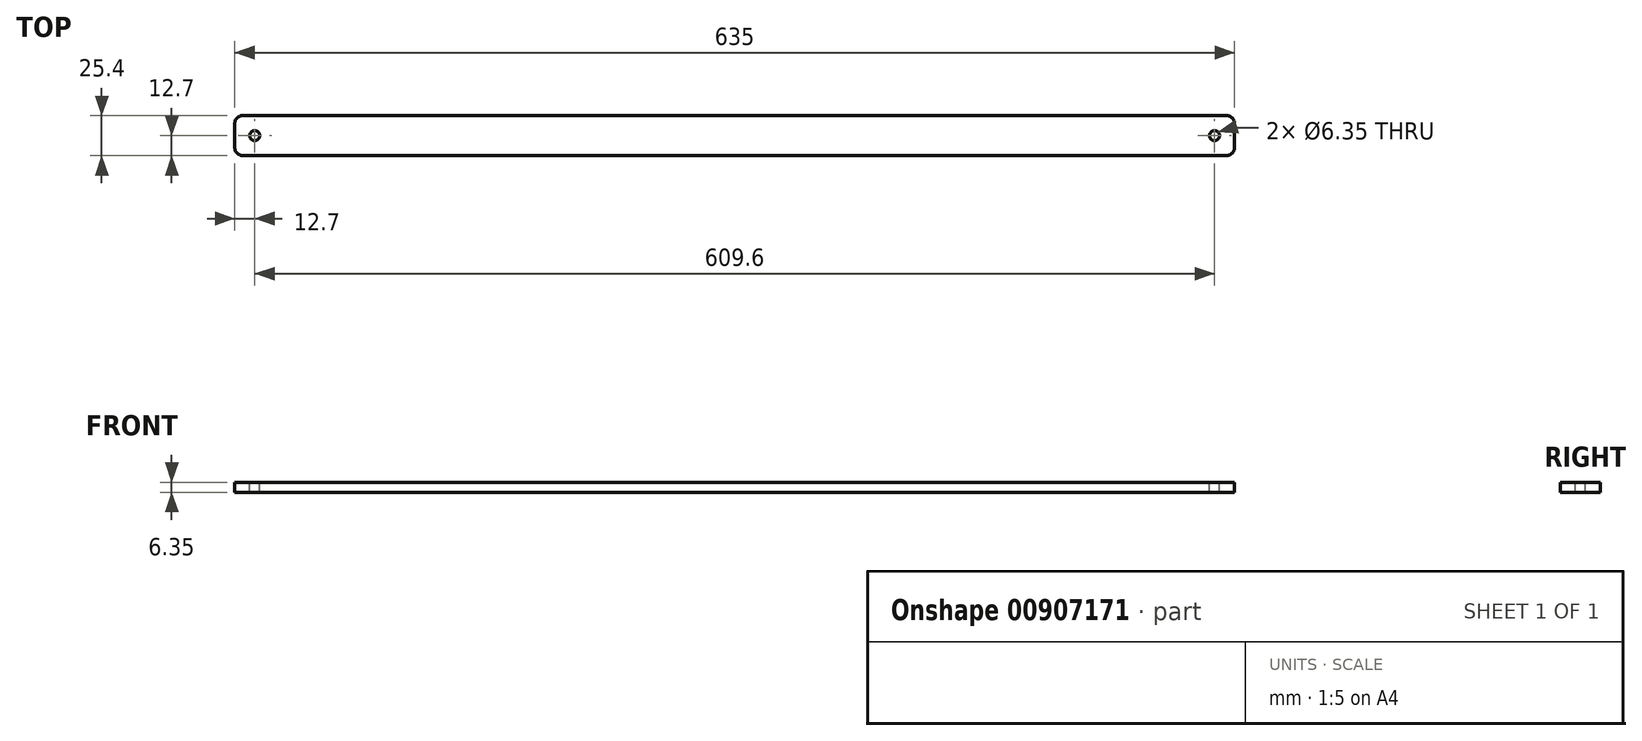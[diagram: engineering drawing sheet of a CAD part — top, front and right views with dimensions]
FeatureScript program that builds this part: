
annotation { "Feature Type Name" : "Feature", "Feature Type Description" : "" }
export const myFeature = defineFeature(function(context is Context, id is Id, definition is map)
    precondition{}
    {
        {
            var Q0;
            Q0=qCreatedBy(makeId("Top.planeOp"),FACE);
            var sketch = newSketch(context, id + "F0", { "sketchPlane" : qUnion([Q0])});
            skLineSegment(sketch, "E0.bottom", {"start": v(5.08, 0) * mm, "end": v(629.92, 0) * mm});
            skLineSegment(sketch, "E0.top", {"start": v(5.08, 25.4) * mm, "end": v(629.92, 25.4) * mm});
            skLineSegment(sketch, "E0.left", {"start": v(0, 5.08) * mm, "end": v(0, 20.32) * mm});
            skLineSegment(sketch, "E0.right", {"start": v(635, 5.08) * mm, "end": v(635, 20.32) * mm});
            skCircle(sketch, "E1", {"center": v(12.7, 12.7) * mm, "radius": 3.18 * mm});
            skCircle(sketch, "E2", {"center": v(622.3, 12.7) * mm, "radius": 3.18 * mm});
            skPoint(sketch, "E3.visualSharp", {"position": v(0, 25.4) * mm});
            skArc(sketch, "E3.filletArc", {"start": v(5.08, 25.4) * mm, "mid": v(1.49, 23.91) * mm, "end": v(0, 20.32) * mm});
            skPoint(sketch, "E4.visualSharp", {"position": v(0, 0) * mm});
            skArc(sketch, "E4.filletArc", {"start": v(0, 5.08) * mm, "mid": v(1.49, 1.49) * mm, "end": v(5.08, 0) * mm});
            skPoint(sketch, "E5.visualSharp", {"position": v(635, 25.4) * mm});
            skArc(sketch, "E5.filletArc", {"start": v(635, 20.32) * mm, "mid": v(633.51, 23.91) * mm, "end": v(629.92, 25.4) * mm});
            skPoint(sketch, "E6.visualSharp", {"position": v(635, 0) * mm});
            skArc(sketch, "E6.filletArc", {"start": v(629.92, 0) * mm, "mid": v(633.51, 1.49) * mm, "end": v(635, 5.08) * mm});
            skSolve(sketch);
        }
        {
            var Q0;
            Q0=makeQuery(id+"F0.imprint","IMPRINT",FACE,{"disambiguationData":[TD([[makeQuery(id+"F0.imprint","IMPRINT",EDGE,{"derivedFrom":sQuery(id+"F0.wireOp",EDGE,"E0.bottom")}),1.0]])]});
            extrude(context, id + "F1", {"entities" : qUnion([Q0]), "oppositeDirection" : true, "depth" : 6.35 * mm, "offsetDistance" : 25.4 * mm});
        }
    });
